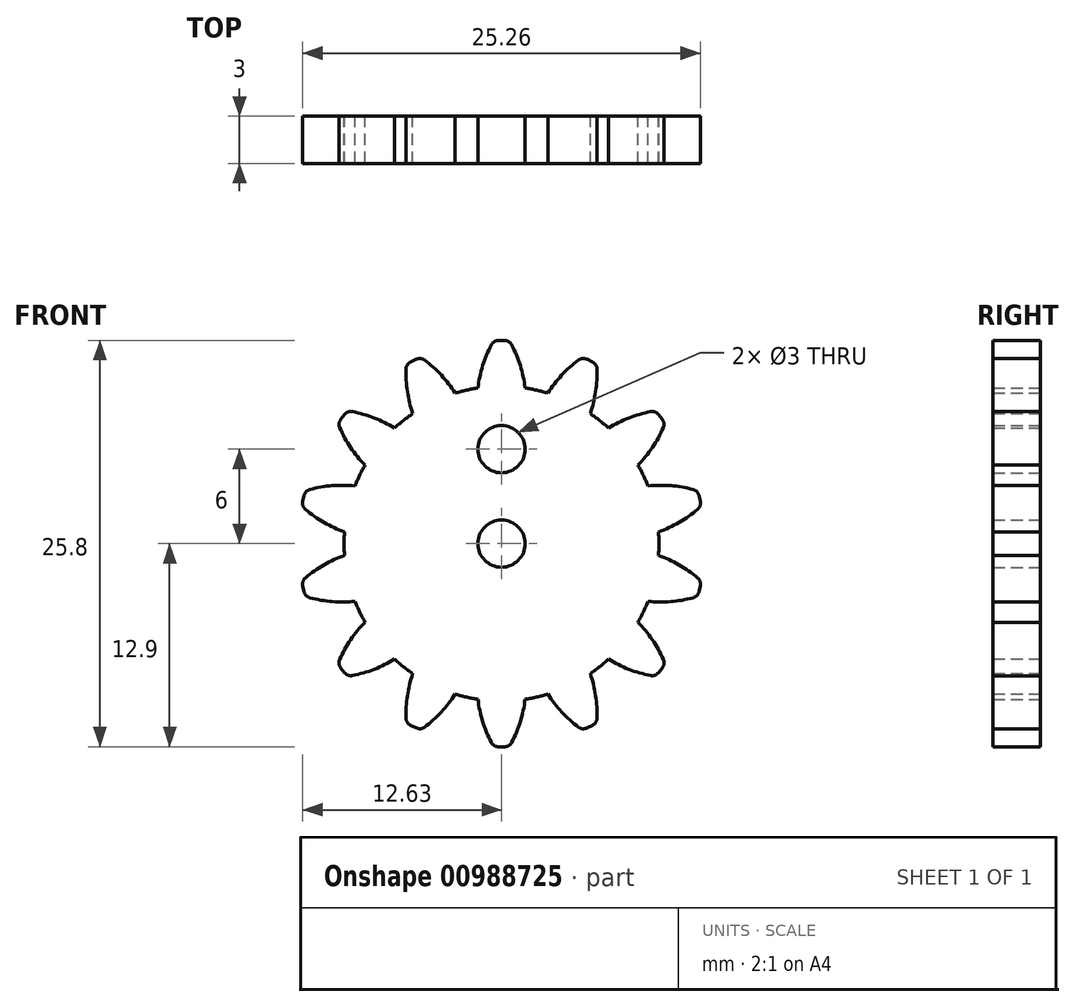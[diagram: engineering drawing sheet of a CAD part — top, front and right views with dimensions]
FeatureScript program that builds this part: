
annotation { "Feature Type Name" : "Feature", "Feature Type Description" : "" }
export const myFeature = defineFeature(function(context is Context, id is Id, definition is map)
    precondition{}
    {
        {
            var Q0;
            Q0=qCreatedBy(makeId("Front.planeOp"),FACE);
            var sketch = newSketch(context, id + "F0", { "sketchPlane" : qUnion([Q0])});
            skCircle(sketch, "E0", {"center": v(0, 0) * mm, "radius": 10 * mm});
            skArc(sketch, "E1", {"start": v(-0.5, 12.9) * mm, "mid": v(-1.15, 11.44) * mm, "end": v(-1.5, 9.89) * mm});
            skArc(sketch, "E2", {"start": v(1.5, 9.89) * mm, "mid": v(1.15, 11.44) * mm, "end": v(0.5, 12.9) * mm});
            skLineSegment(sketch, "E3", {"start": v(-0.5, 12.9) * mm, "end": v(0.5, 12.9) * mm});
            skLineSegment(sketch, "E4", {"start": v(0, 10) * mm, "end": v(0, 12.9) * mm, "construction": true});
            skArc(sketch, "E5.1.0", {"start": v(-2.94, 9.56) * mm, "mid": v(-3.93, 10.8) * mm, "end": v(-5.15, 11.84) * mm});
            skLineSegment(sketch, "E5.1.1", {"start": v(-6.05, 11.4) * mm, "end": v(-5.15, 11.84) * mm});
            skArc(sketch, "E5.1.2", {"start": v(-6.05, 11.4) * mm, "mid": v(-6, 9.81) * mm, "end": v(-5.64, 8.26) * mm});
            skCircle(sketch, "E6", {"center": v(0, 0) * mm, "radius": 1.5 * mm});
            skCircle(sketch, "E7", {"center": v(0, 6) * mm, "radius": 1.5 * mm});
            skLineSegment(sketch, "E8", {"start": v(0, -6) * mm, "end": v(0, 6) * mm});
            skCircle(sketch, "E9", {"center": v(0, 0) * mm, "radius": 6 * mm, "construction": true});
            skArc(sketch, "E10.1.2.0", {"start": v(-6.8, 7.34) * mm, "mid": v(-8.23, 8.03) * mm, "end": v(-9.77, 8.43) * mm});
            skLineSegment(sketch, "E10.4.2.0", {"start": v(-10.4, 7.65) * mm, "end": v(-9.77, 8.43) * mm});
            skArc(sketch, "E10.7.2.0", {"start": v(-10.4, 7.65) * mm, "mid": v(-9.66, 6.24) * mm, "end": v(-8.67, 5) * mm});
            skArc(sketch, "E10.1.3.0", {"start": v(-9.3, 3.66) * mm, "mid": v(-10.9, 3.67) * mm, "end": v(-12.47, 3.36) * mm});
            skLineSegment(sketch, "E10.4.3.0", {"start": v(-12.69, 2.38) * mm, "end": v(-12.47, 3.36) * mm});
            skArc(sketch, "E10.7.3.0", {"start": v(-12.69, 2.38) * mm, "mid": v(-11.41, 1.42) * mm, "end": v(-9.97, 0.74) * mm});
            skArc(sketch, "E10.1.4.0", {"start": v(-9.97, -0.74) * mm, "mid": v(-11.41, -1.42) * mm, "end": v(-12.69, -2.38) * mm});
            skLineSegment(sketch, "E10.4.4.0", {"start": v(-12.47, -3.36) * mm, "end": v(-12.69, -2.38) * mm});
            skArc(sketch, "E10.7.4.0", {"start": v(-12.47, -3.36) * mm, "mid": v(-10.9, -3.67) * mm, "end": v(-9.3, -3.66) * mm});
            skArc(sketch, "E10.1.5.0", {"start": v(-8.67, -5) * mm, "mid": v(-9.66, -6.24) * mm, "end": v(-10.4, -7.65) * mm});
            skLineSegment(sketch, "E10.4.5.0", {"start": v(-9.77, -8.43) * mm, "end": v(-10.4, -7.65) * mm});
            skArc(sketch, "E10.7.5.0", {"start": v(-9.77, -8.43) * mm, "mid": v(-8.23, -8.03) * mm, "end": v(-6.8, -7.34) * mm});
            skArc(sketch, "E10.1.6.0", {"start": v(-5.64, -8.26) * mm, "mid": v(-6, -9.81) * mm, "end": v(-6.05, -11.4) * mm});
            skLineSegment(sketch, "E10.4.6.0", {"start": v(-5.15, -11.84) * mm, "end": v(-6.05, -11.4) * mm});
            skArc(sketch, "E10.7.6.0", {"start": v(-5.15, -11.84) * mm, "mid": v(-3.93, -10.8) * mm, "end": v(-2.94, -9.56) * mm});
            skArc(sketch, "E10.1.7.0", {"start": v(-1.5, -9.89) * mm, "mid": v(-1.15, -11.44) * mm, "end": v(-0.5, -12.9) * mm});
            skLineSegment(sketch, "E10.4.7.0", {"start": v(0.5, -12.9) * mm, "end": v(-0.5, -12.9) * mm});
            skArc(sketch, "E10.7.7.0", {"start": v(0.5, -12.9) * mm, "mid": v(1.15, -11.44) * mm, "end": v(1.5, -9.89) * mm});
            skArc(sketch, "E10.1.8.0", {"start": v(2.94, -9.56) * mm, "mid": v(3.93, -10.8) * mm, "end": v(5.15, -11.84) * mm});
            skLineSegment(sketch, "E10.4.8.0", {"start": v(6.05, -11.4) * mm, "end": v(5.15, -11.84) * mm});
            skArc(sketch, "E10.7.8.0", {"start": v(6.05, -11.4) * mm, "mid": v(6, -9.81) * mm, "end": v(5.64, -8.26) * mm});
            skArc(sketch, "E10.1.9.0", {"start": v(6.8, -7.34) * mm, "mid": v(8.23, -8.03) * mm, "end": v(9.77, -8.43) * mm});
            skLineSegment(sketch, "E10.4.9.0", {"start": v(10.4, -7.65) * mm, "end": v(9.77, -8.43) * mm});
            skArc(sketch, "E10.7.9.0", {"start": v(10.4, -7.65) * mm, "mid": v(9.66, -6.24) * mm, "end": v(8.67, -5) * mm});
            skArc(sketch, "E10.1.10.0", {"start": v(9.3, -3.66) * mm, "mid": v(10.9, -3.67) * mm, "end": v(12.47, -3.36) * mm});
            skLineSegment(sketch, "E10.4.10.0", {"start": v(12.69, -2.38) * mm, "end": v(12.47, -3.36) * mm});
            skArc(sketch, "E10.7.10.0", {"start": v(12.69, -2.38) * mm, "mid": v(11.41, -1.42) * mm, "end": v(9.97, -0.74) * mm});
            skArc(sketch, "E10.1.11.0", {"start": v(9.97, 0.74) * mm, "mid": v(11.41, 1.42) * mm, "end": v(12.69, 2.38) * mm});
            skLineSegment(sketch, "E10.4.11.0", {"start": v(12.47, 3.36) * mm, "end": v(12.69, 2.38) * mm});
            skArc(sketch, "E10.7.11.0", {"start": v(12.47, 3.36) * mm, "mid": v(10.9, 3.67) * mm, "end": v(9.3, 3.66) * mm});
            skArc(sketch, "E10.1.12.0", {"start": v(8.67, 5) * mm, "mid": v(9.66, 6.24) * mm, "end": v(10.4, 7.65) * mm});
            skLineSegment(sketch, "E10.4.12.0", {"start": v(9.77, 8.43) * mm, "end": v(10.4, 7.65) * mm});
            skArc(sketch, "E10.7.12.0", {"start": v(9.77, 8.43) * mm, "mid": v(8.23, 8.03) * mm, "end": v(6.8, 7.34) * mm});
            skArc(sketch, "E10.1.13.0", {"start": v(5.64, 8.26) * mm, "mid": v(6, 9.81) * mm, "end": v(6.05, 11.4) * mm});
            skLineSegment(sketch, "E10.4.13.0", {"start": v(5.15, 11.84) * mm, "end": v(6.05, 11.4) * mm});
            skArc(sketch, "E10.7.13.0", {"start": v(5.15, 11.84) * mm, "mid": v(3.93, 10.8) * mm, "end": v(2.94, 9.56) * mm});
            skSolve(sketch);
        }
        {
            var Q0;
            Q0=makeQuery(id+"F0.imprint","IMPRINT",FACE,{"disambiguationData":[TD([[makeQuery(id+"F0.imprint","IMPRINT",EDGE,{"derivedFrom":sQuery(id+"F0.wireOp",EDGE,"E6")}),-1.0]])]});
            var Q1;
            {var subQ0=sQuery(id+"F0.wireOp",EDGE,"E5.2.0");Q1=makeQuery(id+"F0.imprint","IMPRINT",FACE,{"disambiguationData":[TD([[makeQuery(id+"F0.imprint","IMPRINT",EDGE,{"derivedFrom":subQ0}),1.0]])]});}
            var Q2;
            {var subQ0=sQuery(id+"F0.wireOp",EDGE,"E5.1.0");Q2=makeQuery(id+"F0.imprint","IMPRINT",FACE,{"disambiguationData":[TD([[makeQuery(id+"F0.imprint","IMPRINT",EDGE,{"derivedFrom":subQ0}),1.0]])]});}
            var Q3;
            {var subQ0=sQuery(id+"F0.wireOp",EDGE,"E1");Q3=makeQuery(id+"F0.imprint","IMPRINT",FACE,{"disambiguationData":[TD([[makeQuery(id+"F0.imprint","IMPRINT",EDGE,{"derivedFrom":subQ0}),1.0]])]});}
            var Q4;
            {var subQ0=sQuery(id+"F0.wireOp",EDGE,"E5.14.0");Q4=makeQuery(id+"F0.imprint","IMPRINT",FACE,{"disambiguationData":[TD([[makeQuery(id+"F0.imprint","IMPRINT",EDGE,{"derivedFrom":subQ0}),1.0]])]});}
            var Q5;
            {var subQ0=sQuery(id+"F0.wireOp",EDGE,"E5.13.0");Q5=makeQuery(id+"F0.imprint","IMPRINT",FACE,{"disambiguationData":[TD([[makeQuery(id+"F0.imprint","IMPRINT",EDGE,{"derivedFrom":subQ0}),1.0]])]});}
            var Q6;
            {var subQ0=sQuery(id+"F0.wireOp",EDGE,"E5.12.0");Q6=makeQuery(id+"F0.imprint","IMPRINT",FACE,{"disambiguationData":[TD([[makeQuery(id+"F0.imprint","IMPRINT",EDGE,{"derivedFrom":subQ0}),1.0]])]});}
            var Q7;
            {var subQ0=sQuery(id+"F0.wireOp",EDGE,"E5.11.0");Q7=makeQuery(id+"F0.imprint","IMPRINT",FACE,{"disambiguationData":[TD([[makeQuery(id+"F0.imprint","IMPRINT",EDGE,{"derivedFrom":subQ0}),1.0]])]});}
            var Q8;
            {var subQ0=sQuery(id+"F0.wireOp",EDGE,"E5.10.0");Q8=makeQuery(id+"F0.imprint","IMPRINT",FACE,{"disambiguationData":[TD([[makeQuery(id+"F0.imprint","IMPRINT",EDGE,{"derivedFrom":subQ0}),1.0]])]});}
            var Q9;
            {var subQ0=sQuery(id+"F0.wireOp",EDGE,"E5.9.0");Q9=makeQuery(id+"F0.imprint","IMPRINT",FACE,{"disambiguationData":[TD([[makeQuery(id+"F0.imprint","IMPRINT",EDGE,{"derivedFrom":subQ0}),1.0]])]});}
            var Q10;
            {var subQ0=sQuery(id+"F0.wireOp",EDGE,"E5.8.0");Q10=makeQuery(id+"F0.imprint","IMPRINT",FACE,{"disambiguationData":[TD([[makeQuery(id+"F0.imprint","IMPRINT",EDGE,{"derivedFrom":subQ0}),1.0]])]});}
            var Q11;
            {var subQ0=sQuery(id+"F0.wireOp",EDGE,"E5.7.0");Q11=makeQuery(id+"F0.imprint","IMPRINT",FACE,{"disambiguationData":[TD([[makeQuery(id+"F0.imprint","IMPRINT",EDGE,{"derivedFrom":subQ0}),1.0]])]});}
            var Q12;
            {var subQ0=sQuery(id+"F0.wireOp",EDGE,"E5.6.0");Q12=makeQuery(id+"F0.imprint","IMPRINT",FACE,{"disambiguationData":[TD([[makeQuery(id+"F0.imprint","IMPRINT",EDGE,{"derivedFrom":subQ0}),1.0]])]});}
            var Q13;
            {var subQ0=sQuery(id+"F0.wireOp",EDGE,"E5.5.0");Q13=makeQuery(id+"F0.imprint","IMPRINT",FACE,{"disambiguationData":[TD([[makeQuery(id+"F0.imprint","IMPRINT",EDGE,{"derivedFrom":subQ0}),1.0]])]});}
            var Q14;
            {var subQ0=sQuery(id+"F0.wireOp",EDGE,"E5.4.0");Q14=makeQuery(id+"F0.imprint","IMPRINT",FACE,{"disambiguationData":[TD([[makeQuery(id+"F0.imprint","IMPRINT",EDGE,{"derivedFrom":subQ0}),1.0]])]});}
            var Q15;
            {var subQ0=sQuery(id+"F0.wireOp",EDGE,"E5.3.0");Q15=makeQuery(id+"F0.imprint","IMPRINT",FACE,{"disambiguationData":[TD([[makeQuery(id+"F0.imprint","IMPRINT",EDGE,{"derivedFrom":subQ0}),1.0]])]});}
            var Q16;
            {var subQ0=sQuery(id+"F0.wireOp",EDGE,"E10.1.2.0");Q16=makeQuery(id+"F0.imprint","IMPRINT",FACE,{"disambiguationData":[TD([[makeQuery(id+"F0.imprint","IMPRINT",EDGE,{"derivedFrom":subQ0}),1.0]])]});}
            var Q17;
            {var subQ0=sQuery(id+"F0.wireOp",EDGE,"E10.1.3.0");Q17=makeQuery(id+"F0.imprint","IMPRINT",FACE,{"disambiguationData":[TD([[makeQuery(id+"F0.imprint","IMPRINT",EDGE,{"derivedFrom":subQ0}),1.0]])]});}
            var Q18;
            {var subQ0=sQuery(id+"F0.wireOp",EDGE,"E10.1.4.0");Q18=makeQuery(id+"F0.imprint","IMPRINT",FACE,{"disambiguationData":[TD([[makeQuery(id+"F0.imprint","IMPRINT",EDGE,{"derivedFrom":subQ0}),1.0]])]});}
            var Q19;
            {var subQ0=sQuery(id+"F0.wireOp",EDGE,"E10.1.5.0");Q19=makeQuery(id+"F0.imprint","IMPRINT",FACE,{"disambiguationData":[TD([[makeQuery(id+"F0.imprint","IMPRINT",EDGE,{"derivedFrom":subQ0}),1.0]])]});}
            var Q20;
            {var subQ0=sQuery(id+"F0.wireOp",EDGE,"E10.1.6.0");Q20=makeQuery(id+"F0.imprint","IMPRINT",FACE,{"disambiguationData":[TD([[makeQuery(id+"F0.imprint","IMPRINT",EDGE,{"derivedFrom":subQ0}),1.0]])]});}
            var Q21;
            {var subQ0=sQuery(id+"F0.wireOp",EDGE,"E10.1.7.0");Q21=makeQuery(id+"F0.imprint","IMPRINT",FACE,{"disambiguationData":[TD([[makeQuery(id+"F0.imprint","IMPRINT",EDGE,{"derivedFrom":subQ0}),1.0]])]});}
            var Q22;
            {var subQ0=sQuery(id+"F0.wireOp",EDGE,"E10.1.8.0");Q22=makeQuery(id+"F0.imprint","IMPRINT",FACE,{"disambiguationData":[TD([[makeQuery(id+"F0.imprint","IMPRINT",EDGE,{"derivedFrom":subQ0}),1.0]])]});}
            var Q23;
            {var subQ0=sQuery(id+"F0.wireOp",EDGE,"E10.1.9.0");Q23=makeQuery(id+"F0.imprint","IMPRINT",FACE,{"disambiguationData":[TD([[makeQuery(id+"F0.imprint","IMPRINT",EDGE,{"derivedFrom":subQ0}),1.0]])]});}
            var Q24;
            {var subQ0=sQuery(id+"F0.wireOp",EDGE,"E10.1.10.0");Q24=makeQuery(id+"F0.imprint","IMPRINT",FACE,{"disambiguationData":[TD([[makeQuery(id+"F0.imprint","IMPRINT",EDGE,{"derivedFrom":subQ0}),1.0]])]});}
            var Q25;
            {var subQ0=sQuery(id+"F0.wireOp",EDGE,"E10.1.11.0");Q25=makeQuery(id+"F0.imprint","IMPRINT",FACE,{"disambiguationData":[TD([[makeQuery(id+"F0.imprint","IMPRINT",EDGE,{"derivedFrom":subQ0}),1.0]])]});}
            var Q26;
            {var subQ0=sQuery(id+"F0.wireOp",EDGE,"E10.1.12.0");Q26=makeQuery(id+"F0.imprint","IMPRINT",FACE,{"disambiguationData":[TD([[makeQuery(id+"F0.imprint","IMPRINT",EDGE,{"derivedFrom":subQ0}),1.0]])]});}
            var Q27;
            {var subQ0=sQuery(id+"F0.wireOp",EDGE,"E10.1.13.0");Q27=makeQuery(id+"F0.imprint","IMPRINT",FACE,{"disambiguationData":[TD([[makeQuery(id+"F0.imprint","IMPRINT",EDGE,{"derivedFrom":subQ0}),1.0]])]});}
            extrude(context, id + "F1", {"entities" : qUnion([Q0, Q1, Q2, Q3, Q4, Q5, Q6, Q7, Q8, Q9, Q10, Q11, Q12, Q13, Q14, Q15, Q16, Q17, Q18, Q19, Q20, Q21, Q22, Q23, Q24, Q25, Q26, Q27]), "depth" : 3 * mm, "offsetDistance" : 25 * mm});
        }
        {
            var Q0;
            Q0=makeQuery(id+"F1.opExtrude","SWEPT_EDGE",EDGE,{"disambiguationData":[OSD([sQuery(id+"F0.wireOp",EDGE,"E5.1.0"),sQuery(id+"F0.wireOp",EDGE,"E5.1.1")])]});
            var Q1;
            Q1=makeQuery(id+"F1.opExtrude","SWEPT_EDGE",EDGE,{"disambiguationData":[OSD([sQuery(id+"F0.wireOp",EDGE,"E5.1.1"),sQuery(id+"F0.wireOp",EDGE,"E5.1.2")])]});
            var Q2;
            Q2=makeQuery(id+"F1.opExtrude","SWEPT_EDGE",EDGE,{"disambiguationData":[OSD([sQuery(id+"F0.wireOp",EDGE,"E10.1.2.0"),sQuery(id+"F0.wireOp",EDGE,"E10.4.2.0")])]});
            var Q3;
            Q3=makeQuery(id+"F1.opExtrude","SWEPT_EDGE",EDGE,{"disambiguationData":[OSD([sQuery(id+"F0.wireOp",EDGE,"E10.4.2.0"),sQuery(id+"F0.wireOp",EDGE,"E10.7.2.0")])]});
            var Q4;
            Q4=makeQuery(id+"F1.opExtrude","SWEPT_EDGE",EDGE,{"disambiguationData":[OSD([sQuery(id+"F0.wireOp",EDGE,"E1"),sQuery(id+"F0.wireOp",EDGE,"E3")])]});
            var Q5;
            Q5=makeQuery(id+"F1.opExtrude","SWEPT_EDGE",EDGE,{"disambiguationData":[OSD([sQuery(id+"F0.wireOp",EDGE,"E2"),sQuery(id+"F0.wireOp",EDGE,"E3")])]});
            var Q6;
            Q6=makeQuery(id+"F1.opExtrude","SWEPT_EDGE",EDGE,{"disambiguationData":[OSD([sQuery(id+"F0.wireOp",EDGE,"E10.4.13.0"),sQuery(id+"F0.wireOp",EDGE,"E10.7.13.0")])]});
            var Q7;
            Q7=makeQuery(id+"F1.opExtrude","SWEPT_EDGE",EDGE,{"disambiguationData":[OSD([sQuery(id+"F0.wireOp",EDGE,"E10.1.13.0"),sQuery(id+"F0.wireOp",EDGE,"E10.4.13.0")])]});
            var Q8;
            Q8=makeQuery(id+"F1.opExtrude","SWEPT_EDGE",EDGE,{"disambiguationData":[OSD([sQuery(id+"F0.wireOp",EDGE,"E10.4.12.0"),sQuery(id+"F0.wireOp",EDGE,"E10.7.12.0")])]});
            var Q9;
            Q9=makeQuery(id+"F1.opExtrude","SWEPT_EDGE",EDGE,{"disambiguationData":[OSD([sQuery(id+"F0.wireOp",EDGE,"E10.1.12.0"),sQuery(id+"F0.wireOp",EDGE,"E10.4.12.0")])]});
            var Q10;
            Q10=makeQuery(id+"F1.opExtrude","SWEPT_EDGE",EDGE,{"disambiguationData":[OSD([sQuery(id+"F0.wireOp",EDGE,"E10.4.11.0"),sQuery(id+"F0.wireOp",EDGE,"E10.7.11.0")])]});
            var Q11;
            Q11=makeQuery(id+"F1.opExtrude","SWEPT_EDGE",EDGE,{"disambiguationData":[OSD([sQuery(id+"F0.wireOp",EDGE,"E10.1.11.0"),sQuery(id+"F0.wireOp",EDGE,"E10.4.11.0")])]});
            var Q12;
            Q12=makeQuery(id+"F1.opExtrude","SWEPT_EDGE",EDGE,{"disambiguationData":[OSD([sQuery(id+"F0.wireOp",EDGE,"E10.4.10.0"),sQuery(id+"F0.wireOp",EDGE,"E10.7.10.0")])]});
            var Q13;
            Q13=makeQuery(id+"F1.opExtrude","SWEPT_EDGE",EDGE,{"disambiguationData":[OSD([sQuery(id+"F0.wireOp",EDGE,"E10.1.10.0"),sQuery(id+"F0.wireOp",EDGE,"E10.4.10.0")])]});
            var Q14;
            Q14=makeQuery(id+"F1.opExtrude","SWEPT_EDGE",EDGE,{"disambiguationData":[OSD([sQuery(id+"F0.wireOp",EDGE,"E10.4.9.0"),sQuery(id+"F0.wireOp",EDGE,"E10.7.9.0")])]});
            var Q15;
            Q15=makeQuery(id+"F1.opExtrude","SWEPT_EDGE",EDGE,{"disambiguationData":[OSD([sQuery(id+"F0.wireOp",EDGE,"E10.1.9.0"),sQuery(id+"F0.wireOp",EDGE,"E10.4.9.0")])]});
            var Q16;
            Q16=makeQuery(id+"F1.opExtrude","SWEPT_EDGE",EDGE,{"disambiguationData":[OSD([sQuery(id+"F0.wireOp",EDGE,"E10.4.8.0"),sQuery(id+"F0.wireOp",EDGE,"E10.7.8.0")])]});
            var Q17;
            Q17=makeQuery(id+"F1.opExtrude","SWEPT_EDGE",EDGE,{"disambiguationData":[OSD([sQuery(id+"F0.wireOp",EDGE,"E10.1.8.0"),sQuery(id+"F0.wireOp",EDGE,"E10.4.8.0")])]});
            var Q18;
            Q18=makeQuery(id+"F1.opExtrude","SWEPT_EDGE",EDGE,{"disambiguationData":[OSD([sQuery(id+"F0.wireOp",EDGE,"E10.4.7.0"),sQuery(id+"F0.wireOp",EDGE,"E10.7.7.0")])]});
            var Q19;
            Q19=makeQuery(id+"F1.opExtrude","SWEPT_EDGE",EDGE,{"disambiguationData":[OSD([sQuery(id+"F0.wireOp",EDGE,"E10.1.7.0"),sQuery(id+"F0.wireOp",EDGE,"E10.4.7.0")])]});
            var Q20;
            Q20=makeQuery(id+"F1.opExtrude","SWEPT_EDGE",EDGE,{"disambiguationData":[OSD([sQuery(id+"F0.wireOp",EDGE,"E10.4.6.0"),sQuery(id+"F0.wireOp",EDGE,"E10.7.6.0")])]});
            var Q21;
            Q21=makeQuery(id+"F1.opExtrude","SWEPT_EDGE",EDGE,{"disambiguationData":[OSD([sQuery(id+"F0.wireOp",EDGE,"E10.1.6.0"),sQuery(id+"F0.wireOp",EDGE,"E10.4.6.0")])]});
            var Q22;
            Q22=makeQuery(id+"F1.opExtrude","SWEPT_EDGE",EDGE,{"disambiguationData":[OSD([sQuery(id+"F0.wireOp",EDGE,"E10.1.3.0"),sQuery(id+"F0.wireOp",EDGE,"E10.4.3.0")])]});
            var Q23;
            Q23=makeQuery(id+"F1.opExtrude","SWEPT_EDGE",EDGE,{"disambiguationData":[OSD([sQuery(id+"F0.wireOp",EDGE,"E10.4.3.0"),sQuery(id+"F0.wireOp",EDGE,"E10.7.3.0")])]});
            var Q24;
            Q24=makeQuery(id+"F1.opExtrude","SWEPT_EDGE",EDGE,{"disambiguationData":[OSD([sQuery(id+"F0.wireOp",EDGE,"E10.1.4.0"),sQuery(id+"F0.wireOp",EDGE,"E10.4.4.0")])]});
            var Q25;
            Q25=makeQuery(id+"F1.opExtrude","SWEPT_EDGE",EDGE,{"disambiguationData":[OSD([sQuery(id+"F0.wireOp",EDGE,"E10.4.4.0"),sQuery(id+"F0.wireOp",EDGE,"E10.7.4.0")])]});
            var Q26;
            Q26=makeQuery(id+"F1.opExtrude","SWEPT_EDGE",EDGE,{"disambiguationData":[OSD([sQuery(id+"F0.wireOp",EDGE,"E10.4.5.0"),sQuery(id+"F0.wireOp",EDGE,"E10.7.5.0")])]});
            var Q27;
            Q27=makeQuery(id+"F1.opExtrude","SWEPT_EDGE",EDGE,{"disambiguationData":[OSD([sQuery(id+"F0.wireOp",EDGE,"E10.1.5.0"),sQuery(id+"F0.wireOp",EDGE,"E10.4.5.0")])]});
            fillet(context, id + "F2", {"entities" : qUnion([Q0, Q1, Q2, Q3, Q4, Q5, Q6, Q7, Q8, Q9, Q10, Q11, Q12, Q13, Q14, Q15, Q16, Q17, Q18, Q19, Q20, Q21, Q22, Q23, Q24, Q25, Q26, Q27]), "radius" : .5 * mm, "tangentPropagation" : true, "allowEdgeOverflow" : false});
        }
    });
